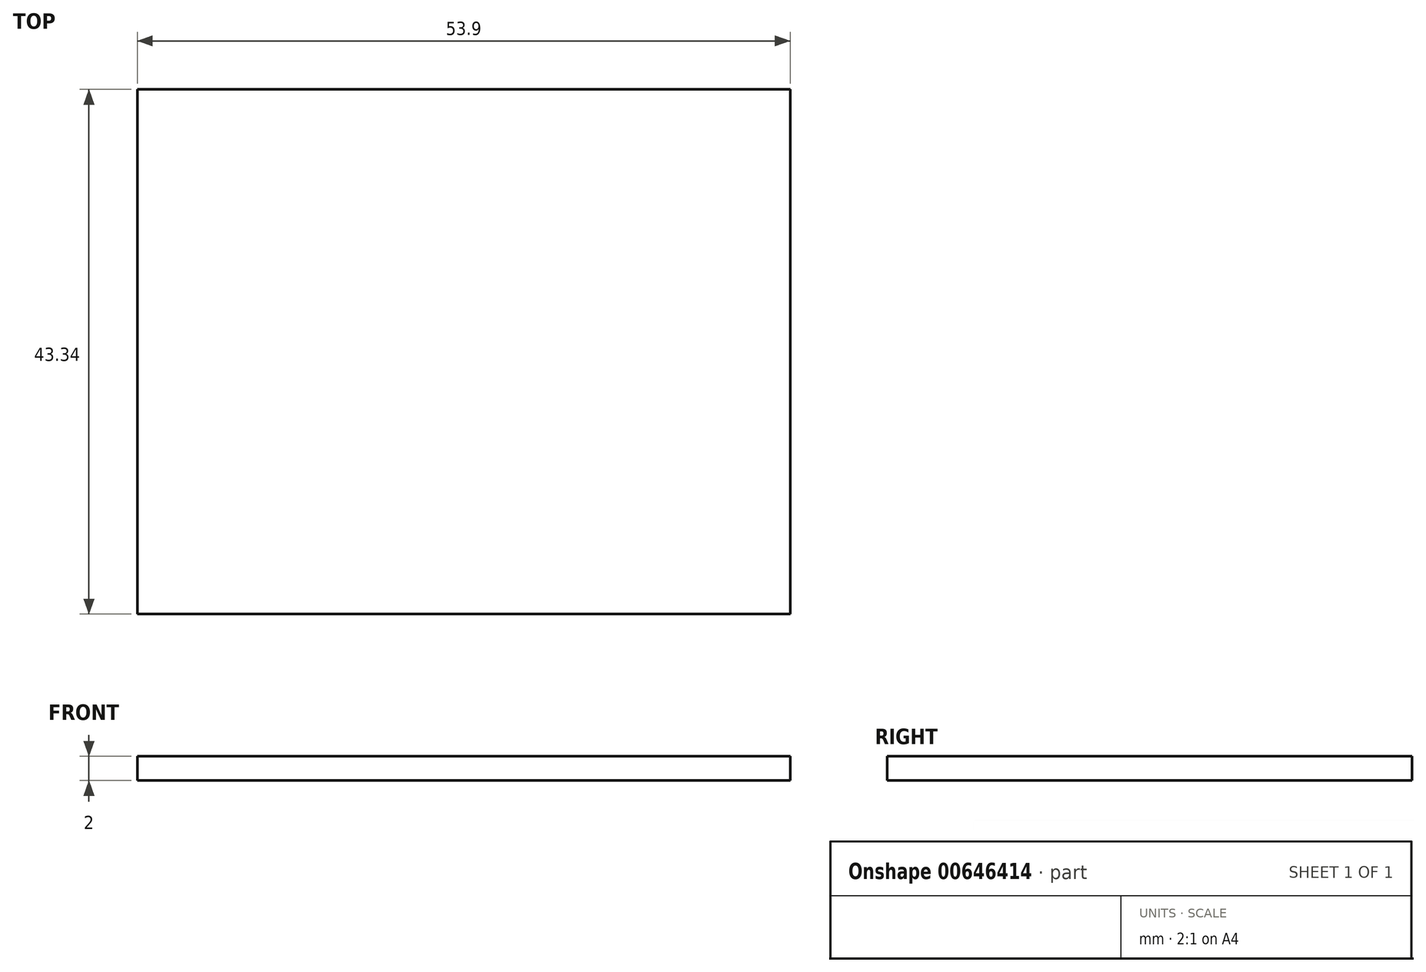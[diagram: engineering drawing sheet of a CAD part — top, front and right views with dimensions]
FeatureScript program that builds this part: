
annotation { "Feature Type Name" : "Feature", "Feature Type Description" : "" }
export const myFeature = defineFeature(function(context is Context, id is Id, definition is map)
    precondition{}
    {
        {
            var Q0;
            Q0=qCreatedBy(makeId("Top.planeOp"),FACE);
            var sketch = newSketch(context, id + "F0", { "sketchPlane" : qUnion([Q0])});
            skLineSegment(sketch, "E0.bottom", {"start": v(0, 0) * mm, "end": v(53.9, 0) * mm});
            skLineSegment(sketch, "E0.top", {"start": v(0, 43.34) * mm, "end": v(53.9, 43.34) * mm});
            skLineSegment(sketch, "E0.left", {"start": v(0, 0) * mm, "end": v(0, 43.34) * mm});
            skLineSegment(sketch, "E0.right", {"start": v(53.9, 0) * mm, "end": v(53.9, 43.34) * mm});
            skSolve(sketch);
        }
        {
            var Q0;
            Q0=makeQuery(id+"F0.imprint","IMPRINT",FACE,{"disambiguationData":[TD([[makeQuery(id+"F0.imprint","IMPRINT",EDGE,{"derivedFrom":sQuery(id+"F0.wireOp",EDGE,"E0.bottom")}),1.0]])]});
            extrude(context, id + "F1", {"entities" : qUnion([Q0]), "depth" : 2 * mm, "offsetDistance" : 25 * mm});
        }
    });
